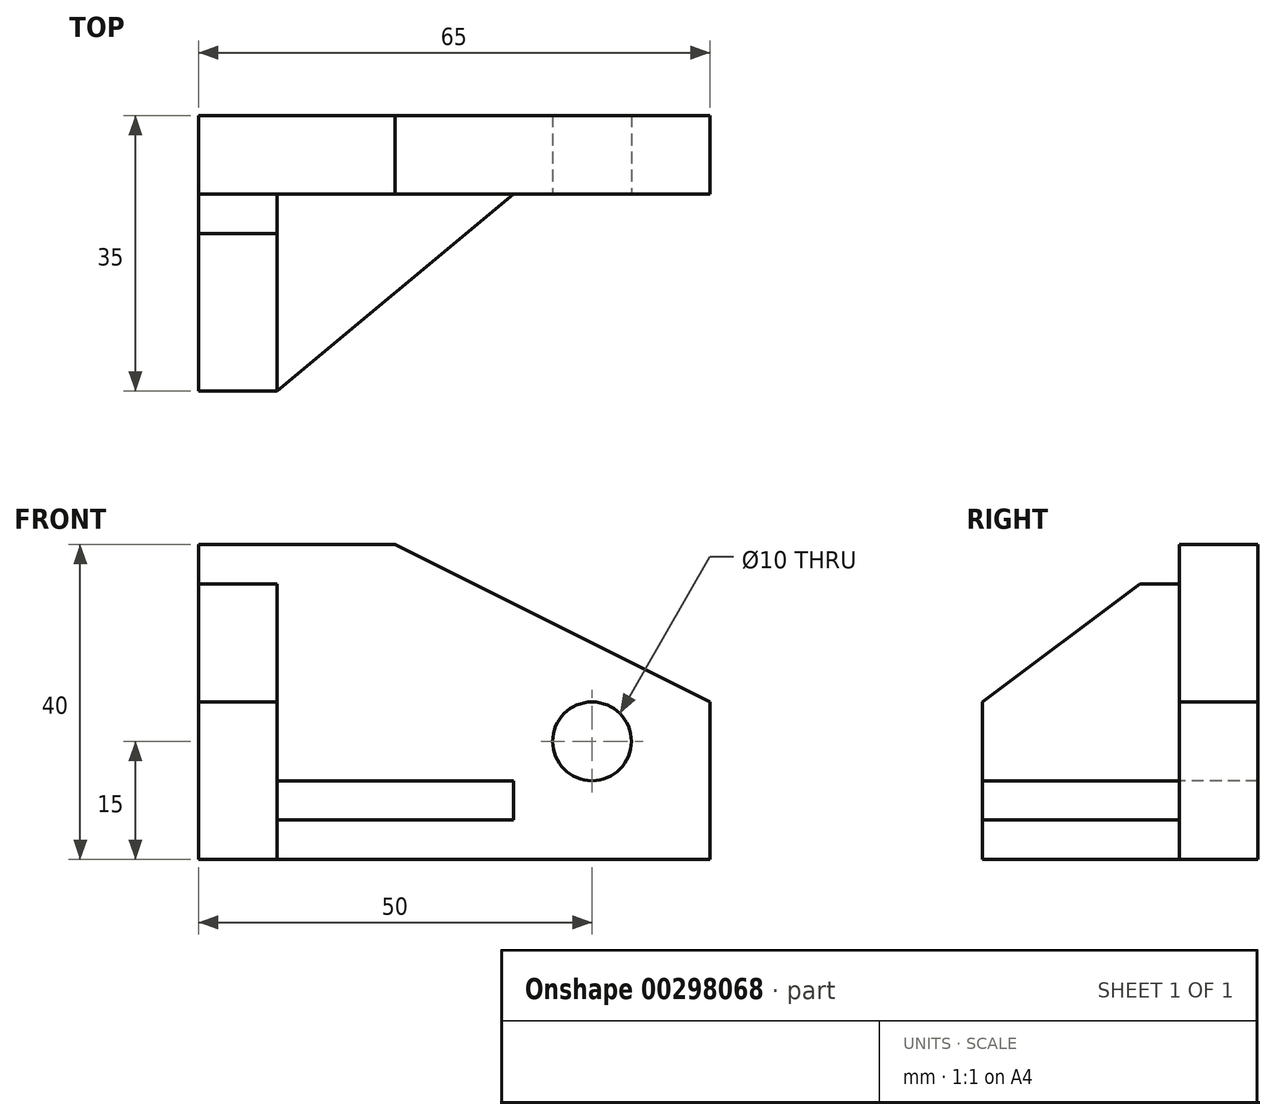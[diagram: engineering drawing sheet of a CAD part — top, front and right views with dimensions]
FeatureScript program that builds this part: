
annotation { "Feature Type Name" : "Feature", "Feature Type Description" : "" }
export const myFeature = defineFeature(function(context is Context, id is Id, definition is map)
    precondition{}
    {
        {
            var Q0;
            Q0=qCreatedBy(makeId("Top.planeOp"),FACE);
            var sketch = newSketch(context, id + "F0", { "sketchPlane" : qUnion([Q0])});
            skLineSegment(sketch, "E0.bottom", {"start": v(-57.57, -18.42) * mm, "end": v(7.43, -18.42) * mm});
            skLineSegment(sketch, "E0.top", {"start": v(-57.57, 16.58) * mm, "end": v(7.43, 16.58) * mm});
            skLineSegment(sketch, "E0.left", {"start": v(-57.57, -18.42) * mm, "end": v(-57.57, 16.58) * mm});
            skLineSegment(sketch, "E0.right", {"start": v(7.43, -18.42) * mm, "end": v(7.43, 16.58) * mm});
            skSolve(sketch);
        }
        {
            var Q0;
            Q0=makeQuery(id+"F0.imprint","IMPRINT",FACE,{"disambiguationData":[TD([[makeQuery(id+"F0.imprint","IMPRINT",EDGE,{"derivedFrom":sQuery(id+"F0.wireOp",EDGE,"E0.bottom")}),1.0]])]});
            extrude(context, id + "F1", {"entities" : qUnion([Q0]), "depth" : 40 * mm});
        }
        {
            var Q0;
            Q0=makeQuery(id+"F1.opExtrude","CAP_FACE",FACE,{"disambiguationData":[OSD([sQuery(id+"F0.wireOp",EDGE,"E0.bottom"),sQuery(id+"F0.wireOp",EDGE,"E0.top"),sQuery(id+"F0.wireOp",EDGE,"E0.left"),sQuery(id+"F0.wireOp",EDGE,"E0.right")])],"isStart":false});
            var sketch = newSketch(context, id + "F2", { "sketchPlane" : qUnion([Q0])});
            skLineSegment(sketch, "E1.bottom", {"start": v(-57.57, 1.58) * mm, "end": v(-47.57, 1.58) * mm});
            skLineSegment(sketch, "E1.top", {"start": v(-57.57, 6.58) * mm, "end": v(-47.57, 6.58) * mm});
            skLineSegment(sketch, "E1.left", {"start": v(-57.57, 1.58) * mm, "end": v(-57.57, 6.58) * mm});
            skLineSegment(sketch, "E1.right", {"start": v(-47.57, 1.58) * mm, "end": v(-47.57, 6.58) * mm});
            skSolve(sketch);
        }
        {
            var Q0;
            Q0=makeQuery(id+"F2.imprint","IMPRINT",FACE,{"disambiguationData":[TD([[makeQuery(id+"F2.imprint","IMPRINT",EDGE,{"derivedFrom":sQuery(id+"F2.wireOp",EDGE,"E1.bottom")}),1.0]])]});
            extrude(context, id + "F3", {"entities" : qUnion([Q0]), "operationType" : NewBodyOperationType.REMOVE, "oppositeDirection" : true, "depth" : 5 * mm});
        }
        {
            var Q0;
            Q0=makeQuery(id+"F1.opExtrude","SWEPT_FACE",FACE,{"disambiguationData":[OSD([sQuery(id+"F0.wireOp",EDGE,"E0.left")])]});
            var sketch = newSketch(context, id + "F4", { "sketchPlane" : qUnion([Q0])});
            skLineSegment(sketch, "E2", {"start": v(-1.58, 35) * mm, "end": v(18.42, 20) * mm});
            skSolve(sketch);
        }
        {
            var Q0;
            {var subQ0=sQuery(id+"F4.wireOp",EDGE,"E2");Q0=makeQuery(id+"F4.imprint","IMPRINT",FACE,{"disambiguationData":[TD([[makeQuery(id+"F4.imprint","IMPRINT",EDGE,{"derivedFrom":subQ0}),1.0]])]});}
            extrude(context, id + "F5", {"entities" : qUnion([Q0]), "operationType" : NewBodyOperationType.REMOVE, "oppositeDirection" : true, "depth" : 65 * mm});
        }
        {
            var Q0;
            Q0=makeQuery(id+"F3.boolean.opBoolean","COPY",FACE,{"derivedFrom":makeQuery(id+"F3.opExtrude","SWEPT_FACE",FACE,{"disambiguationData":[OSD([sQuery(id+"F2.wireOp",EDGE,"E1.right")])]})});
            extrude(context, id + "F6", {"entities" : qUnion([Q0]), "operationType" : NewBodyOperationType.REMOVE, "oppositeDirection" : true, "depth" : 65 * mm});
        }
        {
            var Q0;
            Q0=makeQuery(id+"F1.opExtrude","SWEPT_FACE",FACE,{"disambiguationData":[OSD([sQuery(id+"F0.wireOp",EDGE,"E0.right")])]});
            var sketch = newSketch(context, id + "F7", { "sketchPlane" : qUnion([Q0])});
            skLineSegment(sketch, "E3", {"start": v(6.58, 35) * mm, "end": v(6.58, 0) * mm});
            skLineSegment(sketch, "E4", {"start": v(-18.42, 10) * mm, "end": v(6.58, 10) * mm});
            skLineSegment(sketch, "E5", {"start": v(-18.42, 5) * mm, "end": v(6.58, 5) * mm});
            skSolve(sketch);
        }
        {
            var Q0;
            Q0 = qSketchRegion(id + "F7", true);
            var Q1;
            {var subQ5=sQuery(id+"F7.wireOp",EDGE,"E4");Q1=makeQuery(id+"F7.imprint","IMPRINT",FACE,{"disambiguationData":[TD([[makeQuery(id+"F7.imprint","IMPRINT",EDGE,{"derivedFrom":subQ5}),1.0]])]});}
            var Q2;
            {var subQ4=sQuery(id+"F7.wireOp",EDGE,"E5");Q2=makeQuery(id+"F7.imprint","IMPRINT",FACE,{"disambiguationData":[TD([[makeQuery(id+"F7.imprint","IMPRINT",EDGE,{"derivedFrom":subQ4}),-1.0]])]});}
            extrude(context, id + "F8", {"entities" : qUnion([Q0, Q1, Q2]), "operationType" : NewBodyOperationType.REMOVE, "oppositeDirection" : true, "depth" : 55 * mm});
        }
        {
            var Q0;
            Q0=makeQuery(id+"F1.opExtrude","SWEPT_FACE",FACE,{"disambiguationData":[OSD([sQuery(id+"F0.wireOp",EDGE,"E0.top")])]});
            var sketch = newSketch(context, id + "F9", { "sketchPlane" : qUnion([Q0])});
            skLineSegment(sketch, "E6", {"start": v(32.57, 40) * mm, "end": v(-7.43, 20) * mm});
            skSolve(sketch);
        }
        {
            var Q0;
            {var subQ0=sQuery(id+"F9.wireOp",EDGE,"E6");Q0=makeQuery(id+"F9.imprint","IMPRINT",FACE,{"disambiguationData":[TD([[makeQuery(id+"F9.imprint","IMPRINT",EDGE,{"derivedFrom":subQ0}),-1.0]])]});}
            extrude(context, id + "F10", {"entities" : qUnion([Q0]), "operationType" : NewBodyOperationType.REMOVE, "oppositeDirection" : true, "depth" : 25 * mm});
        }
        {
            var Q0;
            Q0=makeQuery(id+"F8.boolean.opBoolean","COPY",FACE,{"derivedFrom":makeQuery(id+"F8.opExtrude","SWEPT_FACE",FACE,{"disambiguationData":[OSD([sQuery(id+"F7.wireOp",EDGE,"E4")])]})});
            var sketch = newSketch(context, id + "F11", { "sketchPlane" : qUnion([Q0])});
            skLineSegment(sketch, "E7", {"start": v(-47.57, -18.42) * mm, "end": v(-17.57, 6.58) * mm});
            skSolve(sketch);
        }
        {
            var Q0;
            {var subQ0=sQuery(id+"F11.wireOp",EDGE,"E7");Q0=makeQuery(id+"F11.imprint","IMPRINT",FACE,{"disambiguationData":[TD([[makeQuery(id+"F11.imprint","IMPRINT",EDGE,{"derivedFrom":subQ0}),-1.0]])]});}
            extrude(context, id + "F12", {"entities" : qUnion([Q0]), "operationType" : NewBodyOperationType.REMOVE, "oppositeDirection" : true, "depth" : 25 * mm});
        }
        {
            var Q0;
            {var subQ0=sQuery(id+"F7.wireOp",EDGE,"E4");var subQ1=sQuery(id+"F7.wireOp",EDGE,"E3");var subQ2=sQuery(id+"F2.wireOp",EDGE,"E1.right");var subQ3=sQuery(id+"F2.wireOp",EDGE,"E1.top");var subQ4=makeQuery(id+"F6.opExtrude","SWEPT_FACE",FACE,{"disambiguationData":[OSD([subQ3,subQ2])]});var subQ5=sQuery(id+"F0.wireOp",EDGE,"E0.right");Q0=makeQuery(id+"F12.boolean.opBoolean","MERGE",FACE,{"derivedFrom":[makeQuery(id+"F8.boolean.opBoolean","COPY",FACE,{"derivedFrom":makeQuery(id+"F8.opExtrude","SWEPT_FACE",FACE,{"disambiguationData":[OSD([subQ1]),TDD([makeQuery(id+"F7.imprint","IMPRINT",EDGE,{"disambiguationData":[TD([[makeQuery(id+"F7.imprint","INTERSECT",VERTEX,{"derivedFrom":[makeQuery(id+"F1.opExtrude","CAP_EDGE",EDGE,{"disambiguationData":[OSD([subQ5])],"isStart":true}),subQ1]}),1.0]])],"derivedFrom":subQ1})])]})}),makeQuery(id+"F8.boolean.opBoolean","MERGE",FACE,{"derivedFrom":[makeQuery(id+"F6.boolean.opBoolean","MERGE",FACE,{"derivedFrom":[makeQuery(id+"F3.boolean.opBoolean","COPY",FACE,{"derivedFrom":makeQuery(id+"F3.opExtrude","SWEPT_FACE",FACE,{"disambiguationData":[OSD([subQ3])]})}),subQ4]}),makeQuery(id+"F8.opExtrude","SWEPT_FACE",FACE,{"disambiguationData":[OSD([subQ1]),TDD([makeQuery(id+"F7.imprint","IMPRINT",EDGE,{"disambiguationData":[TD([[makeQuery(id+"F7.imprint","INTERSECT",VERTEX,{"derivedFrom":[subQ1,subQ0]}),1.0]])],"derivedFrom":subQ1})])]})]}),makeQuery(id+"F12.opExtrude","SWEPT_FACE",FACE,{"disambiguationData":[OSD([subQ1,subQ0])]})]});}
            var sketch = newSketch(context, id + "F13", { "sketchPlane" : qUnion([Q0])});
            skCircle(sketch, "E8", {"center": v(-7.57, 15) * mm, "radius": 5 * mm});
            skSolve(sketch);
        }
        {
            var Q0;
            Q0=makeQuery(id+"F13.imprint","IMPRINT",FACE,{"disambiguationData":[TD([[makeQuery(id+"F13.imprint","IMPRINT",EDGE,{"derivedFrom":sQuery(id+"F13.wireOp",EDGE,"E8")}),1.0]])]});
            extrude(context, id + "F14", {"entities" : qUnion([Q0]), "operationType" : NewBodyOperationType.REMOVE, "oppositeDirection" : true, "depth" : 25 * mm});
        }
    });
